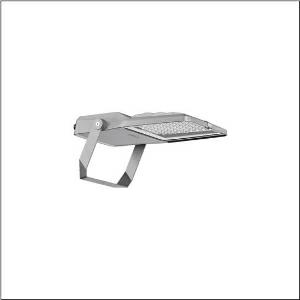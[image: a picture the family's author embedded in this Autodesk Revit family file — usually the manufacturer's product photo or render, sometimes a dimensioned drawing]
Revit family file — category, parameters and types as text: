
# Revit family: floodlight_fl_21_iq_mini___pl64_5xa7771c2e1a_63e9
name_source: partatom
category: Lighting Fixtures
units: mm (PartAtom-declared; Revit-internal decimal feet)

## family parameters
Cut with Voids When Loaded = No
Host = Face
Light Source = No
Part Type = Normal
Room Calculation Point = No
Round Connector Dimension = Use Diameter
Shared = No

## types (1)
- --- (1 x LED, 11790 lm, 87.2 W, 3000K)
    Apparent Load = 87 VA
    CIE Flux Codes = 28 80 98 100 100
    Color Rendering = 70
    Color Temperature = 3000K
    Default Elevation = 1800 mm
    Description = Floodlight FL 21 iQ mini, floodlight, primary light control with lens, of PMMA, primary optical cover: protective disc, of toughened safety glass, transparent, light distribution: PL64, light emission: direct distribution, installation type: surface-mounted, LED, High Power LED, rated luminous flux: 11.790lm, luminous efficacy: 135lm/W, light colour: 730, colour temperature: 3000K, control gear: iQ Comfort/DALI, control: Auto-Match, Temp-Guard, Lumen-Switch, Night-Set, Smart-Wire, Light-Fading, Desk-Remote (wireless, voltage-free reading and setting of iQ features in the workshop via application-optimized NFC function/RFID function), optimised constant luminous flux control (CLO 2.0), with terminal, 6-pole, mains connection: 220..240V, AC, 50/60Hz, start of lifetime: 87W, end of service life: 92W, reduction: 40W, luminaire housing, of diecast aluminium, powder-coated, Siteco® metallic grey (DB 702S), corrosivity category C5 mid according to DIN EN ISO 12944, suitable for swimming pools, chlorine-resistant, sealing non-destructively replaceable, mounting bracket, of steel, galvanised, powder-coated, Siteco® metallic grey (DB 702S), protection rating (complete): IP66, insulation class (complete): insulation class II (safety insulation), certification: CE, ENEC, VDE, protection symbol: D, impact resistance: IK08, permissible operating ambient temperature: -40..+40°C, permissible operating ambient temperature for outdoor applications: -40..+50°C, standard: DIN EN 12944, LABS conformity tested according to VDMA 24364:2018-05, packaging unit: 1 piece

Light Distribution: PL64
    Height = 70 mm
    Lamp = 1 x LED
    Lamp Light Flux = 11790 lm
    Lamp Power = 87.2 W
    Lamp count = 1
    Length = 485 mm
    Luminous efficacy = 135 lm/W
    Manufacturer = Siteco
    ModVariant = No
    Model = 5XA7771C2E1A
    Number of Poles = 1
    OnlyDefault = Yes
    Power Factor = 1
    Product Name = Floodlight FL 21 iQ mini | PL64
    Product group = floodlight | pylon annexe
    ProductGroupID = 6200
    Protection Class = Protection class II
    Protection Degree = IP 66
    RLX_Detail_Level = 1
    RLX_Emergency_Light_Flux = 0 lm
    RLX_Emergency_Type = 0
    RLX_Emergency_Type_DB = No
    RlxData = <blob elided: 96297 chars, md5=d09cf075>
    Socket = socket
    Standby Power = 0 W
    System Light Flux = 11790 lm
    System Power = 87 W
    Type Comments = factory setting: luminous flux: 100 % | dim-lin: 254 | 456 mA
    Type Image = l_1006845.jpg
    URL = http://relux.com
    VarID = @adj_166686
    Voltage = 0 V
    Weight = 0.00 kg
    Width = 337 mm

## geometry (parser evidence)
native form markers: Blend x4, Sweep x13
no freeform markers — native parametric forms only
